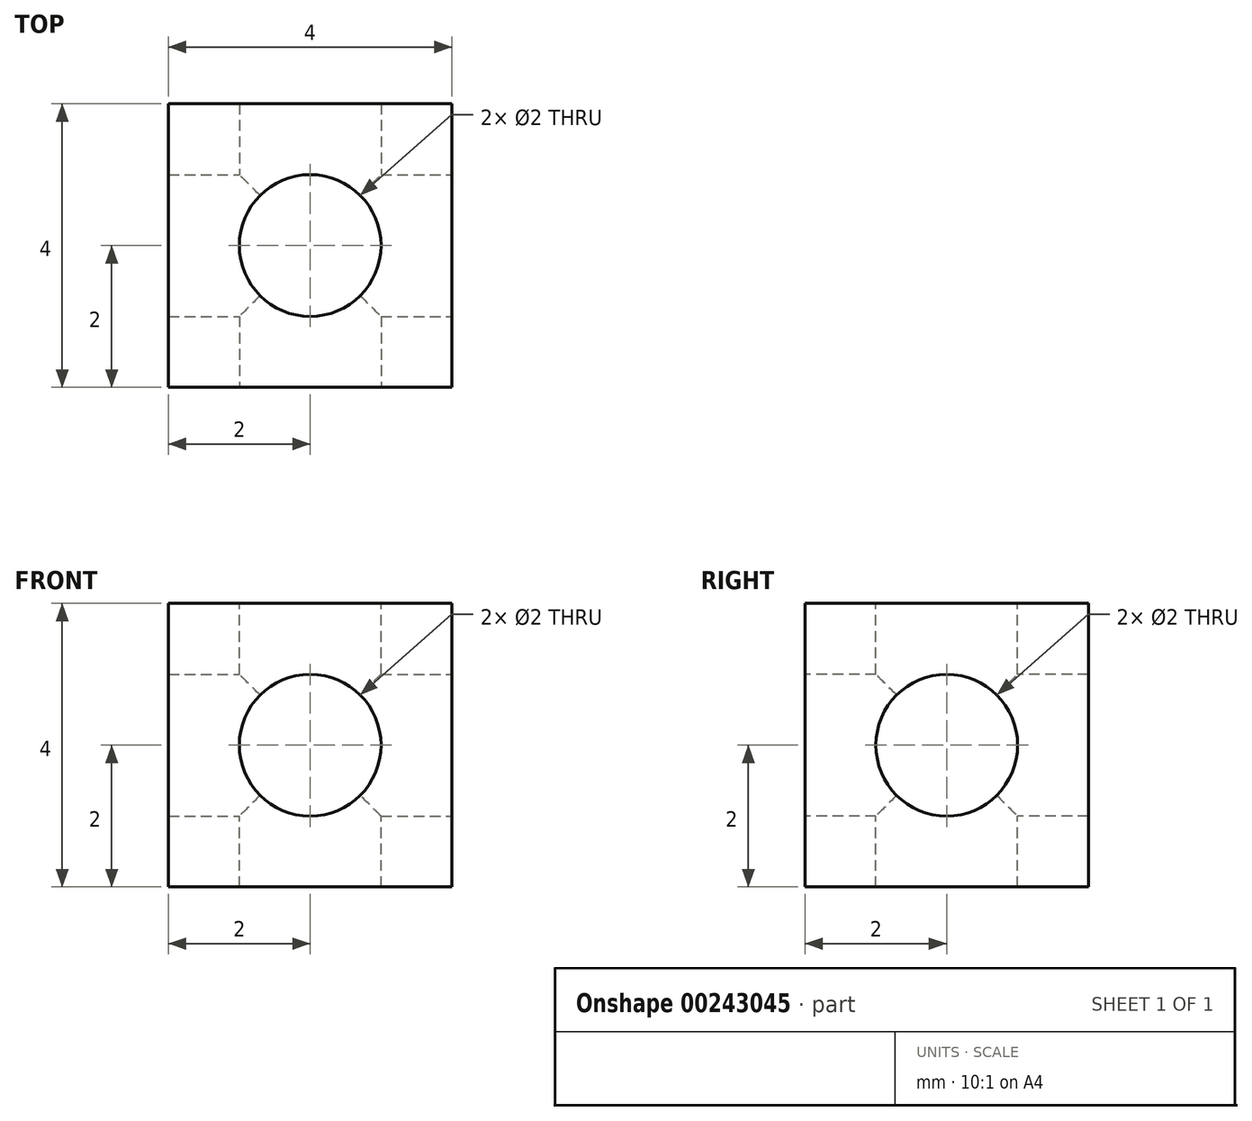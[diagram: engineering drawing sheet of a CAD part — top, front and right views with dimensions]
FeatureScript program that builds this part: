
annotation { "Feature Type Name" : "Feature", "Feature Type Description" : "" }
export const myFeature = defineFeature(function(context is Context, id is Id, definition is map)
    precondition{}
    {
        {
            var Q0;
            Q0=qCreatedBy(makeId("Top.planeOp"),FACE);
            var sketch = newSketch(context, id + "F0", { "sketchPlane" : qUnion([Q0])});
            skLineSegment(sketch, "E0.bottom", {"start": v(0, 0) * mm, "end": v(4, 0) * mm});
            skLineSegment(sketch, "E0.top", {"start": v(0, 4) * mm, "end": v(4, 4) * mm});
            skLineSegment(sketch, "E0.left", {"start": v(0, 0) * mm, "end": v(0, 4) * mm});
            skLineSegment(sketch, "E0.right", {"start": v(4, 0) * mm, "end": v(4, 4) * mm});
            skSolve(sketch);
        }
        {
            var Q0;
            Q0 = qSketchRegion(id + "F0", true);
            extrude(context, id + "F1", {"entities" : qUnion([Q0]), "depth" : 4 * mm});
        }
        {
            var Q0;
            Q0=makeQuery(id+"F1.opExtrude","CAP_FACE",FACE,{"disambiguationData":[OSD([sQuery(id+"F0.wireOp",EDGE,"E0.bottom"),sQuery(id+"F0.wireOp",EDGE,"E0.top"),sQuery(id+"F0.wireOp",EDGE,"E0.left"),sQuery(id+"F0.wireOp",EDGE,"E0.right")])],"isStart":false});
            var sketch = newSketch(context, id + "F2", { "sketchPlane" : qUnion([Q0])});
            skCircle(sketch, "E1", {"center": v(2, 2) * mm, "radius": 1 * mm});
            skPoint(sketch, "E1.centerSnap0", {"position": v(2, 0) * mm});
            skPoint(sketch, "E1.centerSnap1", {"position": v(0, 2) * mm});
            skSolve(sketch);
        }
        {
            var Q0;
            Q0 = qSketchRegion(id + "F2", true);
            extrude(context, id + "F3", {"entities" : qUnion([Q0]), "operationType" : NewBodyOperationType.REMOVE, "oppositeDirection" : true, "depth" : 25 * mm});
        }
        {
            var Q0;
            Q0=makeQuery(id+"F1.opExtrude","SWEPT_FACE",FACE,{"disambiguationData":[OSD([sQuery(id+"F0.wireOp",EDGE,"E0.bottom")])]});
            var sketch = newSketch(context, id + "F4", { "sketchPlane" : qUnion([Q0])});
            skCircle(sketch, "E2", {"center": v(2, 2) * mm, "radius": 1 * mm});
            skPoint(sketch, "E2.centerSnap0", {"position": v(2, 0) * mm});
            skPoint(sketch, "E2.centerSnap1", {"position": v(0, 2) * mm});
            skSolve(sketch);
        }
        {
            var Q0;
            Q0 = qSketchRegion(id + "F4", true);
            extrude(context, id + "F5", {"entities" : qUnion([Q0]), "operationType" : NewBodyOperationType.REMOVE, "oppositeDirection" : true, "depth" : 25 * mm});
        }
        {
            var Q0;
            Q0=makeQuery(id+"F1.opExtrude","SWEPT_FACE",FACE,{"disambiguationData":[OSD([sQuery(id+"F0.wireOp",EDGE,"E0.right")])]});
            var sketch = newSketch(context, id + "F6", { "sketchPlane" : qUnion([Q0])});
            skCircle(sketch, "E3", {"center": v(2, 2) * mm, "radius": 1 * mm});
            skPoint(sketch, "E3.centerSnap0", {"position": v(0, 2) * mm});
            skPoint(sketch, "E3.centerSnap1", {"position": v(2, 4) * mm});
            skSolve(sketch);
        }
        {
            var Q0;
            Q0 = qSketchRegion(id + "F6", true);
            extrude(context, id + "F7", {"entities" : qUnion([Q0]), "operationType" : NewBodyOperationType.REMOVE, "oppositeDirection" : true, "depth" : 25 * mm});
        }
    });
